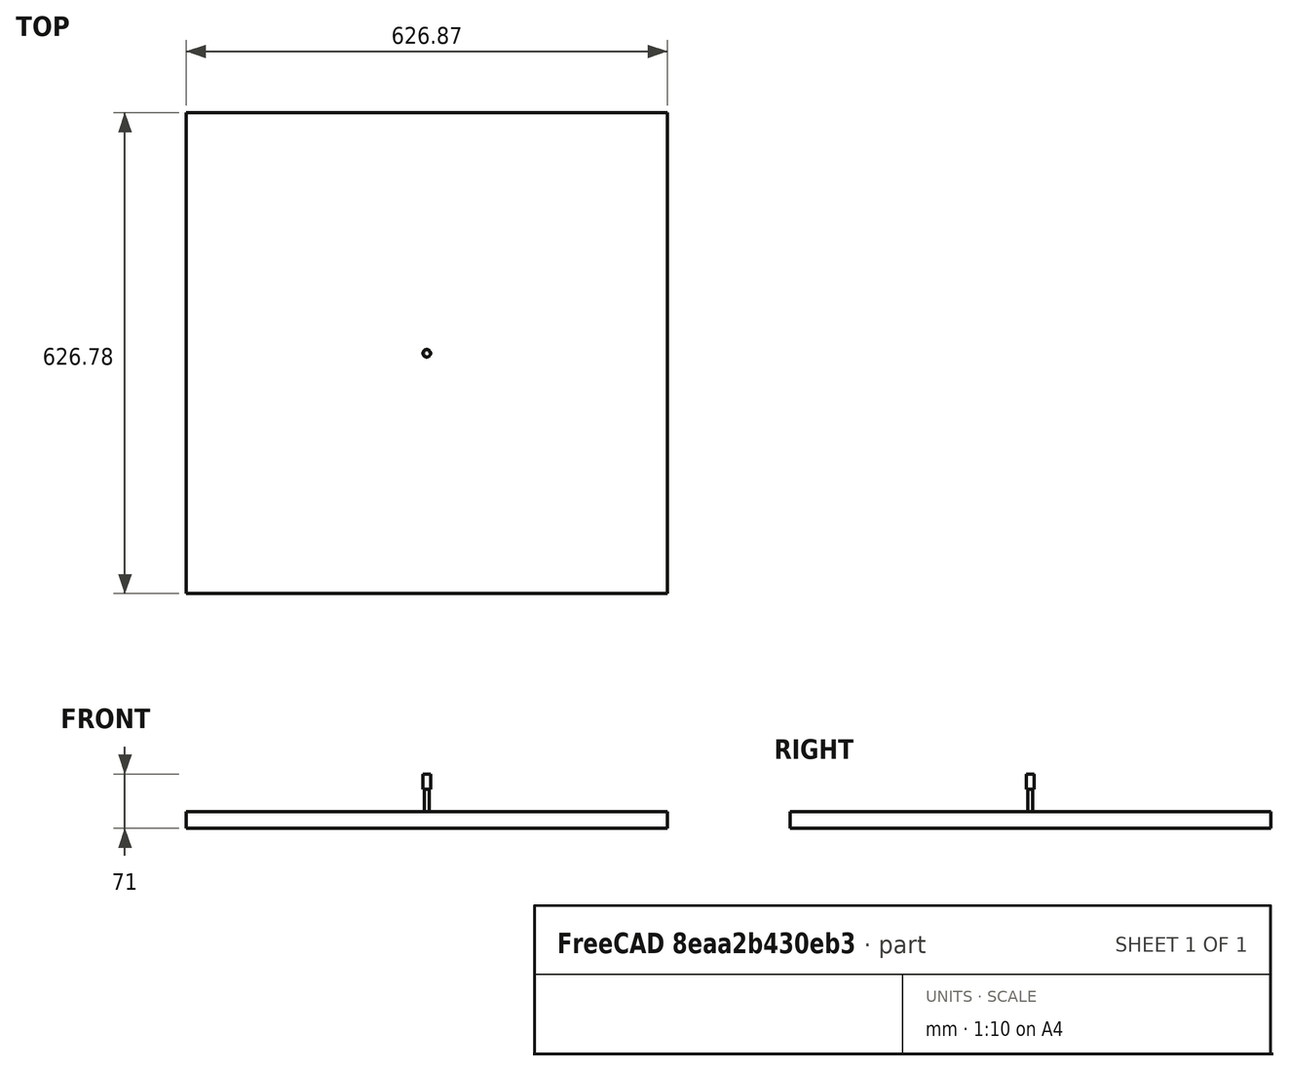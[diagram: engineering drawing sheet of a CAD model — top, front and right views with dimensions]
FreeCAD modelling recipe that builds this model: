
FCSTD DOCUMENT  (FreeCAD 0.19R14555 (Git shallow))
Label: BarrenTop
License: All rights reserved
LicenseURL: http://en.wikipedia.org/wiki/All_rights_reserved
objects: Part::FeaturePython×3, Path::FeaturePython×3, App::DocumentObjectGroup×2, Sketcher::SketchObject×1, PartDesign::Pad×1, PartDesign::Fillet×1, PartDesign::Body×1, App::FeaturePython×1, Path::FeatureCompoundPython×1, Mesh::FeaturePython×1
note: 10 computed .brp shape members not serialized (recipe doc carries the construction recipe); baked Part::Feature solids carry a one-line shape summary decoded from their .brp

FEATURE [Sketcher::SketchObject] Sketch
  FullyConstrained = true
  MapMode = 5
  Support = -> [XY_Plane]
  sketch-geometry (1):
    g0: Circle CenterX=0 CenterY=0 CenterZ=0 NormalX=0 NormalY=0 NormalZ=1 AngleXU=0 Radius=312.5
  constraints (2):
    c: Coincident(g0,g-1)
    c: Diameter(g0) = 625
FEATURE [PartDesign::Pad] Pad
  Direction = (1,1,1)
  Length = 20
  Length2 = 100
  Profile = -> Sketch
  Reversed = true
  Type = 0
FEATURE [PartDesign::Fillet] Fillet
  Base = -> Pad [Edge2]
  BaseFeature = -> Pad
  Radius = 5
  SupportTransform = false
FEATURE [PartDesign::Body] Body
  Group = -> [Sketch,Pad,Fillet]
  Origin = -> Origin
  Tip = -> Fillet
FEATURE [App::FeaturePython] SetupSheet  # Path/CAM operation (typed FeaturePython)
  ClearanceHeightExpression = OpStockZMax+SetupSheet.ClearanceHeightOffset
  ClearanceHeightOffset = 5
  CoolantMode = 0
  CoolantModes = None | Flood | Mist
  FinalDepthExpression = OpFinalDepth
  HorizRapid = 0
  SafeHeightExpression = OpStockZMax+SetupSheet.SafeHeightOffset
  SafeHeightOffset = 3
  StartDepthExpression = OpStartDepth
  StepDownExpression = OpToolDiameter
  VertRapid = 0
FEATURE [Part::FeaturePython] Clone  label="Model-Body"  # Draft clone (typed FeaturePython)
  AttacherType = Attacher::AttachEngine3D
  Fuse = false
  Objects = -> [Body]
  PathResource = Model
  Scale = (1,1,1)
FEATURE [App::DocumentObjectGroup] Model
  Group = -> [Clone]
FEATURE [Part::FeaturePython] Stock  # WARN: FeaturePython — macro-defined, semantics opaque (R4)
  Base = -> Model
  ExtXneg = 1
  ExtXpos = 1
  ExtYneg = 1
  ExtYpos = 1
  ExtZneg = 1
  ExtZpos = 1
  Placement = pos=(-312.375,-312.389,-20) rot=(0,0,1;0rad)
  StockType = FromBase
FEATURE [Part::FeaturePython] ToolBit001  label="6.4mm Endmill"  # Path/CAM toolbit (typed FeaturePython)
  BitPropertyNames = Chipload | CuttingEdgeHeight | Diameter | Flutes | Length | Material | ShankDiameter
  BitShape = /app/freecad/Mod/Path/Tools/Shape/endmill.fcstd
  Chipload = 0
  CuttingEdgeHeight = 30
  Diameter = 6.4
  File = <userpath>/Documents/MensShed/FreeCAD/Bit/6.4mm_Endmill.fctb
  Flutes = 0
  Length = 50
  Material = 0
  ShankDiameter = 10
  ShapeName = endmill
FEATURE [Path::FeaturePython] __4mm_Endmill  label="6.4mm Endmill001"  # Path/CAM operation (typed FeaturePython)
  HorizFeed = 40
  HorizRapid = 0
  SpindleDir = 0
  SpindleSpeed = 10000
  Tool = -> ToolBit001
  ToolNumber = 2
  VertFeed = 40
  VertRapid = 0
  expr: VertRapid = SetupSheet.VertRapid
  expr: HorizRapid = SetupSheet.HorizRapid
FEATURE [App::DocumentObjectGroup] Tools
  Group = -> [__4mm_Endmill]
FEATURE [Path::FeaturePython] Profile  # Path/CAM operation (typed FeaturePython)
  Active = true
  AreaParams:
    Tolerance = 1e-07
    FitArcs = True
    Simplify = False
    CleanDistance = 0.0
    Accuracy = 0.01
    Unit = 1.0
    MinArcPoints = 4
    MaxArcPoints = 100
    ClipperScale = 10000000.0
    Fill = 0
    Coplanar = 0
    Reorient = True
    Outline = False
    Explode = False
    OpenMode = 0
    Deflection = 0.01
    SubjectFill = 0
    ClipFill = 0
    Offset = 3.2
    ExtraPass = 0
    Stepover = 0.0
    LastStepover = 0.0
    JoinType = 0
    EndType = 0
    MiterLimit = 2.0
    RoundPrecision = 0.0
    PocketMode = 0
    ToolRadius = 1.0
    PocketExtraOffset = 0.0
    PocketStepover = 0.0
    PocketLastStepover = 0.0
    FromCenter = False
    Angle = 45.0
    AngleShift = 0.0
    Shift = 0.0
    Thicken = False
    SectionCount = -1
    Stepdown = 1.0
    SectionOffset = 0.0
    SectionTolerance = 1e-06
    SectionMode = 2
    Project = False
  AttemptInverseAngle = true
  Base = -> [Clone]
  ClearanceHeight = 6
  CoolantMode = None
  CycleTime = 00:01:47
  Direction = 0
  EnableRotation = 0
  FinalDepth = -8
  HandleMultipleFeatures = 0
  InverseAngle = false
  JoinType = 0
  LimitDepthToFace = true
  MiterLimit = 0.1
  OffsetExtra = 0
  OpFinalDepth = -5
  OpStartDepth = 1
  OpStockZMax = 1
  OpStockZMin = -21
  OpToolDiameter = 6.4
  PathParams = {'orientation': 1, 'feedrate': 40.0, 'feedrate_v': 40.0, 'verbose': True, 'resume_height': 4.0, 'retraction': 6.0, 'return_end': True, 'preamble': False}
  ReverseDirection = false
  SafeHeight = 4
  Side = 0
  StartDepth = 0
  StartPoint = (0,0,0)
  StepDown = 6.4
  ToolController = -> __4mm_Endmill
  UseComp = true
  UseStartPoint = false
  processCircles = false
  processHoles = false
  processPerimeter = true
  expr: StartDepth = 0
  expr: FinalDepth = -8
  expr: StepDown = OpToolDiameter
  expr: SafeHeight = OpStockZMax + SetupSheet.SafeHeightOffset
  expr: ClearanceHeight = OpStockZMax + SetupSheet.ClearanceHeightOffset
FEATURE [Path::FeatureCompoundPython] Operations  # Path/CAM operation (typed FeaturePython)
  Group = -> [Profile]
  UsePlacements = false
FEATURE [Path::FeaturePython] Job  # Path/CAM operation (typed FeaturePython)
  CycleTime = 00:01:47
  Fixtures = G54
  GeometryTolerance = 0.01
  LastPostProcessDate = 2022-01-19 10:56:38.045283
  LastPostProcessOutput = <userpath>/Documents/MensShed/BarrenTop.ngc
  Model = -> Model
  Operations = -> Operations
  OrderOutputBy = 0
  PostProcessor = 7
  PostProcessorOutputFile = <userpath>/Documents/MensShed/BarrenTop.ngc
  SetupSheet = -> SetupSheet
  SplitOutput = false
  Stock = -> Stock
  Tools = -> Tools
FEATURE [Mesh::FeaturePython] CutMaterial  # WARN: FeaturePython — macro-defined, semantics opaque (R4)
